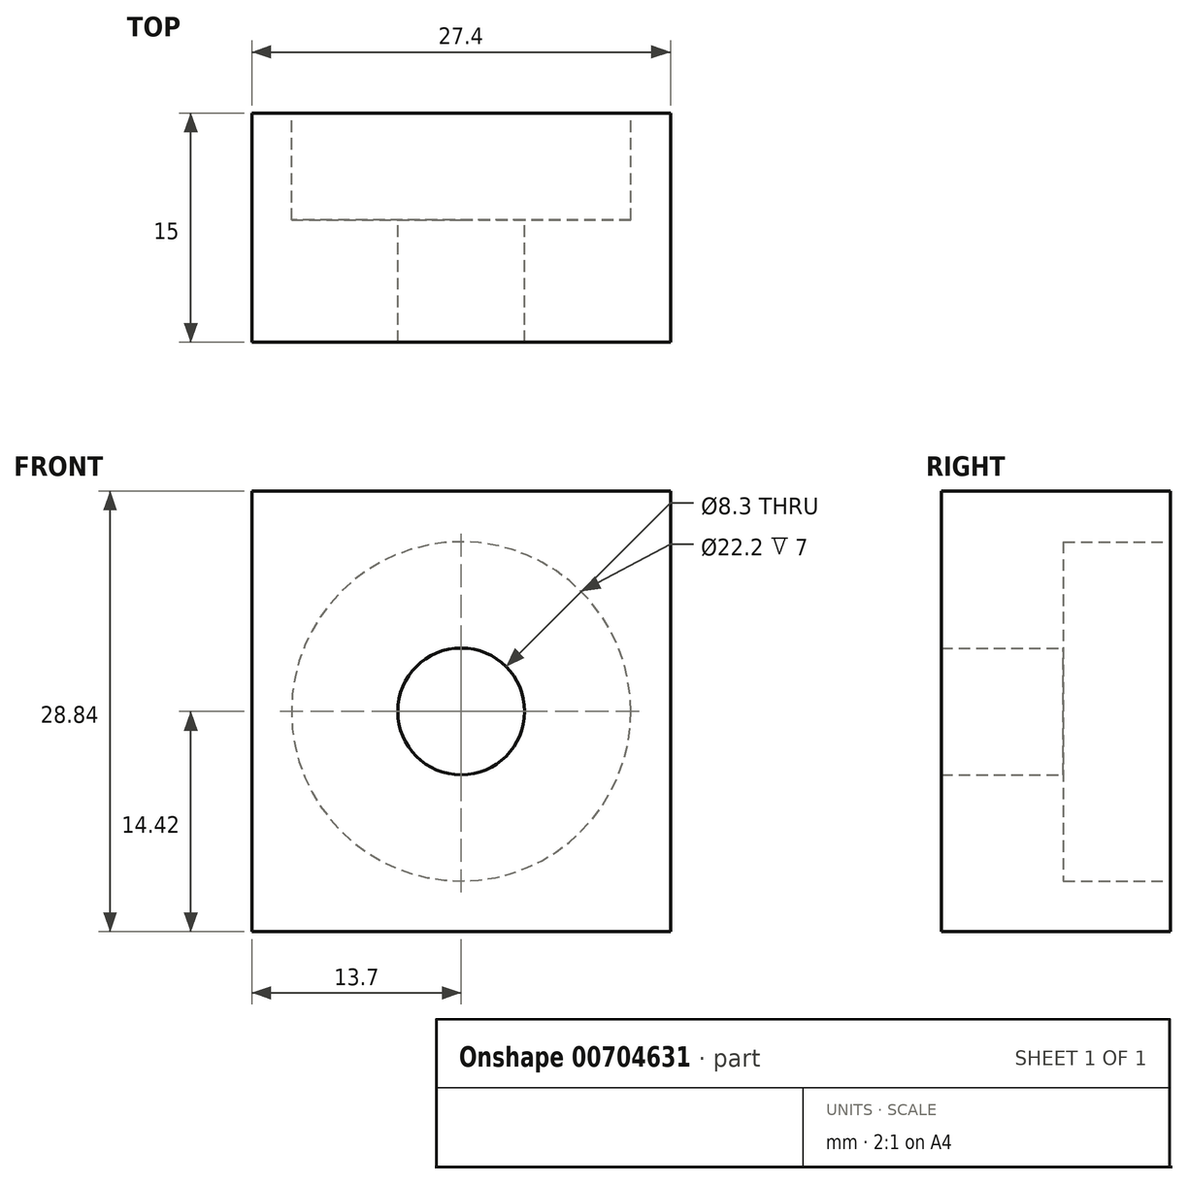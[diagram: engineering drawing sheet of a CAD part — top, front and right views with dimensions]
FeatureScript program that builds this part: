
annotation { "Feature Type Name" : "Feature", "Feature Type Description" : "" }
export const myFeature = defineFeature(function(context is Context, id is Id, definition is map)
    precondition{}
    {
        {
            var Q0;
            Q0=qCreatedBy(makeId("Front.planeOp"),FACE);
            var sketch = newSketch(context, id + "F0", { "sketchPlane" : qUnion([Q0])});
            skLineSegment(sketch, "E0.bottom", {"start": v(-13.7, 14.42) * mm, "end": v(13.7, 14.42) * mm});
            skLineSegment(sketch, "E0.top", {"start": v(-13.7, -14.42) * mm, "end": v(13.7, -14.42) * mm});
            skLineSegment(sketch, "E0.left", {"start": v(-13.7, 14.42) * mm, "end": v(-13.7, -14.42) * mm});
            skLineSegment(sketch, "E0.right", {"start": v(13.7, 14.42) * mm, "end": v(13.7, -14.42) * mm});
            skPoint(sketch, "E0.middle", {"position": v(0, 0) * mm});
            skCircle(sketch, "E1", {"center": v(0, 0) * mm, "radius": 4.15 * mm});
            skCircle(sketch, "E2", {"center": v(0, 0) * mm, "radius": 11.1 * mm});
            skSolve(sketch);
        }
        {
            var Q0;
            Q0=makeQuery(id+"F0.imprint","IMPRINT",FACE,{"disambiguationData":[TD([[makeQuery(id+"F0.imprint","IMPRINT",EDGE,{"derivedFrom":sQuery(id+"F0.wireOp",EDGE,"E0.bottom")}),-1.0]])]});
            var Q1;
            Q1=makeQuery(id+"F0.imprint","IMPRINT",FACE,{"disambiguationData":[TD([[makeQuery(id+"F0.imprint","IMPRINT",EDGE,{"derivedFrom":sQuery(id+"F0.wireOp",EDGE,"E1")}),-1.0]])]});
            extrude(context, id + "F1", {"entities" : qUnion([Q0, Q1]), "depth" : 15 * mm, "offsetDistance" : 25 * mm});
        }
        {
            var Q0;
            Q0=makeQuery(id+"F1.opExtrude","CAP_FACE",FACE,{"disambiguationData":[OSD([sQuery(id+"F0.wireOp",EDGE,"E0.bottom"),sQuery(id+"F0.wireOp",EDGE,"E0.top"),sQuery(id+"F0.wireOp",EDGE,"E0.left"),sQuery(id+"F0.wireOp",EDGE,"E0.right"),sQuery(id+"F0.wireOp",EDGE,"E1")])],"isStart":true});
            var sketch = newSketch(context, id + "F2", { "sketchPlane" : qUnion([Q0])});
            skCircle(sketch, "E3", {"center": v(0, 0) * mm, "radius": 11.1 * mm});
            skSolve(sketch);
        }
        {
            var Q0;
            Q0=makeQuery(id+"F2.imprint","IMPRINT",FACE,{"disambiguationData":[TD([[makeQuery(id+"F2.imprint","IMPRINT",EDGE,{"derivedFrom":sQuery(id+"F2.wireOp",EDGE,"E3")}),1.0]])]});
            extrude(context, id + "F3", {"entities" : qUnion([Q0]), "operationType" : NewBodyOperationType.REMOVE, "oppositeDirection" : true, "depth" : 7 * mm, "offsetDistance" : 25 * mm});
        }
    });
